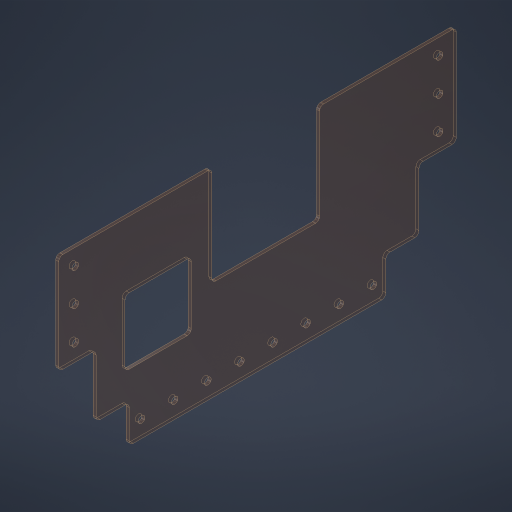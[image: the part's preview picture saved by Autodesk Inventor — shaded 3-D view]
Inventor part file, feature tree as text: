
AUTODESK INVENTOR PART (.ipt)
format: ipt  version: 2023.4 (Build 274418000, 418)  size: 306,176 bytes
history: native  units: in
note: dims shown in document units (in); Inventor stores cm internally (conversion verified against a paired STEP export)
features: sketch x3, extrude x2, fillet x2, projected_geometry x2, hole x1
ambient origin geometry x8: Origin, YZ Plane, XZ Plane, XY Plane, X Axis, Y Axis, Z Axis, Center Point
bodies: Solid1 (feature_tree)
feature tree (10):
  extrude  "Extrusion1"  Depth=12.0in
  fillet  "Fillet1"  Radius=2.0in
  hole  "Hole1"  [1 undecoded]
  extrude  "Extrusion2"  Depth=0.125in
  fillet  "Fillet2"  Radius=0.5in
  sketch  "Sketch1"  dims[d0=6.0in d1=12.0in d2=2.0in]
  sketch  "Sketch2"  dims[d3=3.0in d4=3.0in]
  sketch  "Sketch3"  dims[d5=0.09in d6=0.0in d7=0.125in d8=0.5in d9=0.5in d10=0.5in d11=2.3622in d13=1.0in d14=0.3937in d16=1.0in d18=0.201in d19=0.75in d20=0.385in d21=0.25in d22=0.5635in d23=1.0in d24=0.8108in d25=1.125in d26=3.0in d27=1.125in d28=2.125in d29=0.09in d30=0.0in d31=0.125in d32=4.7244in d34=1.0in d35=0.3937in d37=1.0in d39=3.0in d40=3.25in d41=5.75in]
  projected_geometry  "Project Cut Edges1"
  projected_geometry  "Project Cut Edges2"
note: 1 required parameter value undecoded (feature->parameter linkage not recoverable at this tier; creation-order binding heuristic only, values carry confidence <= 0.55)
